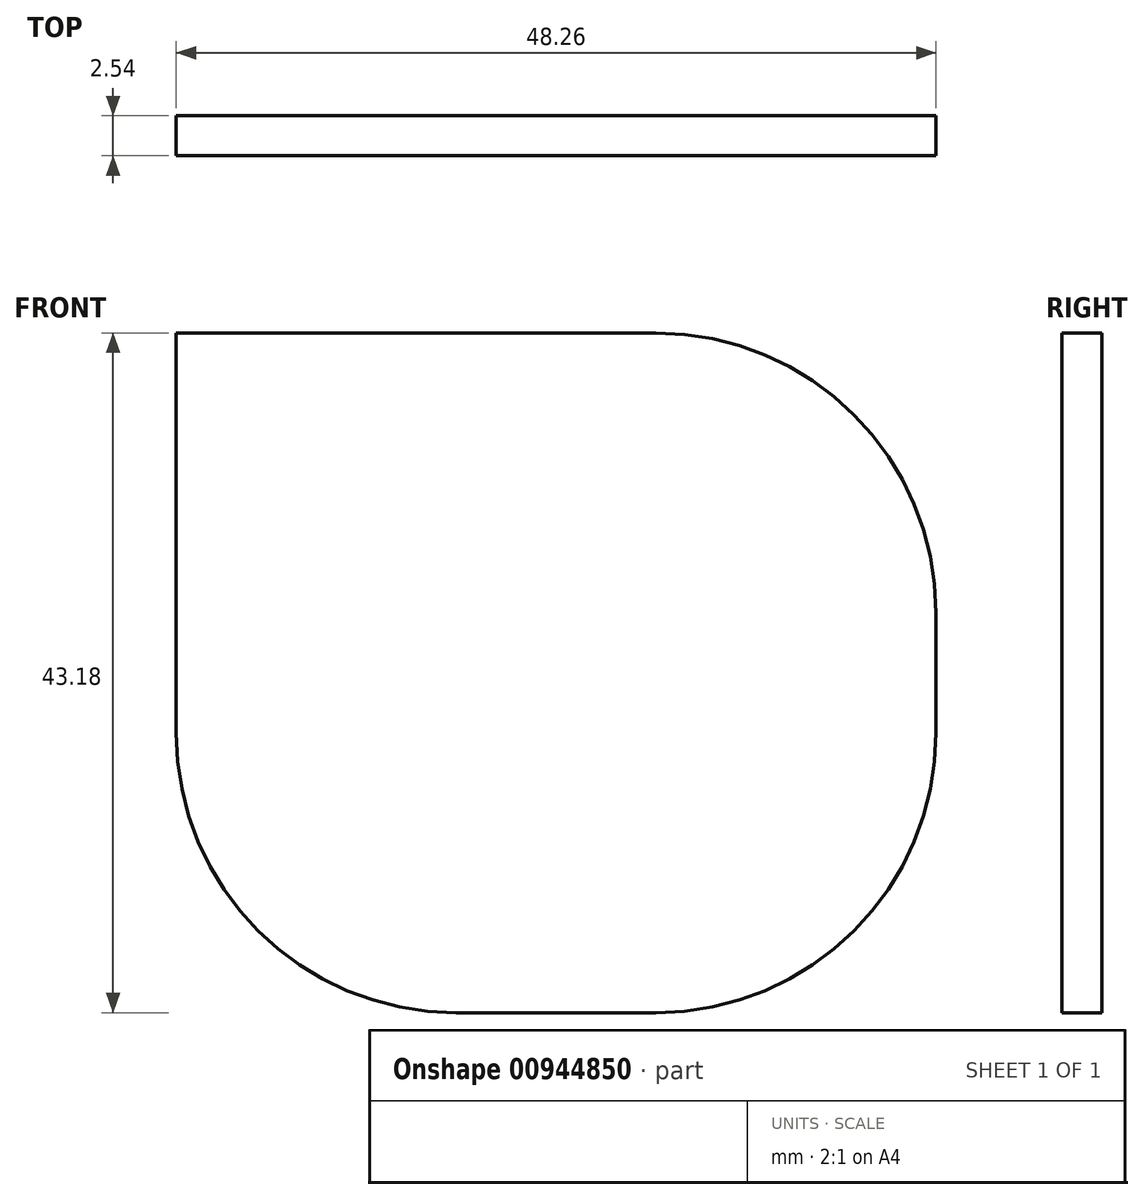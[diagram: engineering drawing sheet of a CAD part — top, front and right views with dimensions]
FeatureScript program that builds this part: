
annotation { "Feature Type Name" : "Feature", "Feature Type Description" : "" }
export const myFeature = defineFeature(function(context is Context, id is Id, definition is map)
    precondition{}
    {
        {
            var Q0;
            Q0=qCreatedBy(makeId("Front.planeOp"),FACE);
            var sketch = newSketch(context, id + "F0", { "sketchPlane" : qUnion([Q0])});
            skLineSegment(sketch, "E0.bottom", {"start": v(-24.13, 21.59) * mm, "end": v(24.13, 21.59) * mm});
            skLineSegment(sketch, "E0.top", {"start": v(-24.13, -21.59) * mm, "end": v(24.13, -21.59) * mm});
            skLineSegment(sketch, "E0.left", {"start": v(-24.13, 21.59) * mm, "end": v(-24.13, -21.6) * mm});
            skLineSegment(sketch, "E0.right", {"start": v(24.13, 21.59) * mm, "end": v(24.13, -21.6) * mm});
            skPoint(sketch, "E0.middle", {"position": v(0, 0) * mm});
            skSolve(sketch);
        }
        {
            var Q0;
            Q0=makeQuery(id+"F0.imprint","IMPRINT",FACE,{"disambiguationData":[TD([[makeQuery(id+"F0.imprint","IMPRINT",EDGE,{"derivedFrom":sQuery(id+"F0.wireOp",EDGE,"E0.bottom")}),-1.0]])]});
            extrude(context, id + "F1", {"entities" : qUnion([Q0]), "depth" : 2.54 * mm, "offsetDistance" : 25.4 * mm});
        }
        {
            var Q0;
            Q0=makeQuery(id+"F1.opExtrude","SWEPT_EDGE",EDGE,{"disambiguationData":[OSD([sQuery(id+"F0.wireOp",EDGE,"E0.top"),sQuery(id+"F0.wireOp",EDGE,"E0.right")])]});
            var Q1;
            Q1=makeQuery(id+"F1.opExtrude","SWEPT_EDGE",EDGE,{"disambiguationData":[OSD([sQuery(id+"F0.wireOp",EDGE,"E0.top"),sQuery(id+"F0.wireOp",EDGE,"E0.left")])]});
            fillet(context, id + "F2", {"entities" : qUnion([Q0, Q1]), "radius" : 17.78 * mm, "tangentPropagation" : true, "allowEdgeOverflow" : false});
        }
        {
            var Q0;
            Q0=makeQuery(id+"F1.opExtrude","SWEPT_EDGE",EDGE,{"disambiguationData":[OSD([sQuery(id+"F0.wireOp",EDGE,"E0.bottom"),sQuery(id+"F0.wireOp",EDGE,"E0.right")])]});
            fillet(context, id + "F3", {"entities" : qUnion([Q0]), "radius" : 17.78 * mm, "tangentPropagation" : true, "allowEdgeOverflow" : false});
        }
    });
